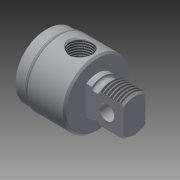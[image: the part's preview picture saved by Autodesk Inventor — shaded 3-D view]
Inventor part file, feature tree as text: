
AUTODESK INVENTOR PART (.ipt)
format: ipt  version: 2014 SP2 (Build 180246200, 246)  size: 295,424 bytes
history: native  units: in
note: dims shown in document units (in); Inventor stores cm internally (conversion verified against a paired STEP export)
features: other x154, sketch x7, revolve x4, thread x2, extrude x2, hole x1
ambient origin geometry x8: Origin, YZ Plane, XZ Plane, XY Plane, X Axis, Y Axis, Z Axis, Center Point
bodies: Solid1 (feature_tree)
feature tree (170):
  revolve  "Revolution1"  Angle=360.0deg
  revolve  "Revolution2"  [1 undecoded]
  thread  "Thread1"  [1 undecoded]
  extrude  "Extrusion1"  TaperAngle=360.0deg  [1 undecoded]
  hole  "Hole1"  [1 undecoded]
  revolve  "Revolution3"  [1 undecoded]
  thread  "Thread2"  [1 undecoded]
  revolve  "Revolution4"  [1 undecoded]
  extrude  "Extrusion2"  [1 undecoded]
  other  "1_XY"
  other  "1_YZ"
  other  "1_ZX"
  other  "1_X"
  other  "1_Y"
  other  "1_Z"
  other  "1_Center"
  other  "c1_XY"
  other  "c1_YZ"
  other  "c1_ZX"
  other  "c1_X"
  other  "c1_Y"
  other  "c1_Z"
  other  "c1_Center"
  other  "c2_XY"
  other  "c2_YZ"
  other  "c2_ZX"
  other  "c2_X"
  other  "c2_Y"
  other  "c2_Z"
  other  "c2_Center"
  other  "cc1_XY"
  other  "cc1_YZ"
  other  "cc1_ZX"
  other  "cc1_X"
  other  "cc1_Y"
  other  "cc1_Z"
  other  "cc1_Center"
  other  "cc2_XY"
  other  "cc2_YZ"
  other  "cc2_ZX"
  other  "cc2_X"
  other  "cc2_Y"
  other  "cc2_Z"
  other  "cc2_Center"
  other  "lovra1_XY"
  other  "lovra1_YZ"
  other  "lovra1_ZX"
  other  "lovra1_X"
  other  "lovra1_Y"
  other  "lovra1_Z"
  other  "lovra1_Center"
  other  "lovra2_XY"
  other  "lovra2_YZ"
  other  "lovra2_ZX"
  other  "lovra2_X"
  other  "lovra2_Y"
  other  "lovra2_Z"
  other  "lovra2_Center"
  other  "lovra21_XY"
  other  "lovra21_YZ"
  other  "lovra21_ZX"
  other  "lovra21_X"
  other  "lovra21_Y"
  other  "lovra21_Z"
  other  "lovra21_Center"
  other  "lovra22_XY"
  other  "lovra22_YZ"
  other  "lovra22_ZX"
  other  "lovra22_X"
  other  "lovra22_Y"
  other  "lovra22_Z"
  other  "lovra22_Center"
  other  "lovra3_XY"
  other  "lovra3_YZ"
  other  "lovra3_ZX"
  other  "lovra3_X"
  other  "lovra3_Y"
  other  "lovra3_Z"
  other  "lovra3_Center"
  other  "olen_XY"
  other  "olen_YZ"
  other  "olen_ZX"
  other  "olen_X"
  other  "olen_Y"
  other  "olen_Z"
  other  "olen_Center"
  other  "p1_XY"
  other  "p1_YZ"
  other  "p1_ZX"
  other  "p1_X"
  other  "p1_Y"
  other  "p1_Z"
  other  "p1_Center"
  other  "p2_XY"
  other  "p2_YZ"
  other  "p2_ZX"
  other  "p2_X"
  other  "p2_Y"
  other  "p2_Z"
  other  "p2_Center"
  other  "port_XY"
  other  "port_YZ"
  other  "port_ZX"
  other  "port_X"
  other  "port_Y"
  other  "port_Z"
  other  "port_Center"
  other  "port2_XY"
  other  "port2_YZ"
  other  "port2_ZX"
  other  "port2_X"
  other  "port2_Y"
  other  "port2_Z"
  other  "port2_Center"
  other  "thd1_XY"
  other  "thd1_YZ"
  other  "thd1_ZX"
  other  "thd1_X"
  other  "thd1_Y"
  other  "thd1_Z"
  other  "thd1_Center"
  other  "thd2_XY"
  other  "thd2_YZ"
  other  "thd2_ZX"
  other  "thd2_X"
  other  "thd2_Y"
  other  "thd2_Z"
  other  "thd2_Center"
  other  "to_mounting_bracket_XY"
  other  "to_mounting_bracket_YZ"
  other  "to_mounting_bracket_ZX"
  other  "to_mounting_bracket_X"
  other  "to_mounting_bracket_Y"
  other  "to_mounting_bracket_Z"
  other  "to_mounting_bracket_Center"
  other  "to_nut_XY"
  other  "to_nut_YZ"
  other  "to_nut_ZX"
  other  "to_nut_X"
  other  "to_nut_Y"
  other  "to_nut_Z"
  other  "to_nut_Center"
  other  "to_pin_XY"
  other  "to_pin_YZ"
  other  "to_pin_ZX"
  other  "to_pin_X"
  other  "to_pin_Y"
  other  "to_pin_Z"
  other  "to_pin_Center"
  other  "to_screw_XY"
  other  "to_screw_YZ"
  other  "to_screw_ZX"
  other  "to_screw_X"
  other  "to_screw_Y"
  other  "to_screw_Z"
  other  "to_screw_Center"
  other  "to_tube_XY"
  other  "to_tube_YZ"
  other  "to_tube_ZX"
  other  "to_tube_X"
  other  "to_tube_Y"
  other  "to_tube_Z"
  other  "to_tube_Center"
  sketch  "Sketch_18"  dims[d14=0.2481in d15=0.0in d16=360.0deg]
  sketch  "Sketch_15"  dims[d6=0.375in d7=0.75in d8=0.375in d9=0.25in d10=0.5635in d11=0.825in d12=120.0deg d13=360.0deg]
  sketch  "Sketch_9"  dims[d2=0.3547in d3=0.0in d4=0.625in d5=0.0in]
  sketch  "Sketch4"  dims[d0=360.0deg d1=360.0deg]
  sketch  "Sketch_47"
  sketch  "Sketch_24"  dims[d17=0.5587in d18=0.0in]
  sketch  "Sketch_43"  dims[d19=0.0in d20=0.0in d21=0.0in d22=0.0in d23=0.0in d24=0.0in d25=0.0in d26=0.0in]
note: 8 required parameter values undecoded (feature->parameter linkage not recoverable at this tier; creation-order binding heuristic only, values carry confidence <= 0.55)